# Revit family: Shower-Valve_Trim-KOHLER-K-26347T_1
name_source: partatom
category: Specialty Equipment
revit_build: Autodesk Revit 2017 (Build: 20160225_1515(x64)
units: mm (PartAtom-declared; Revit-internal decimal feet)

## family parameters
Cut with Voids When Loaded = No
Host = Face
OmniClass Number = 23.31.25.00
OmniClass Title = Toilet and Bath Specialties
Part Type = Normal
Room Calculation Point = No
Round Connector Dimension = Use Diameter
Shared = No

## types (6) — shared parameters
ADA Compliant = No
Assembly Code = C1030200
Date Modified = 02/12/2021
Default Elevation = 42"
Description = RECESSED THERMOSTATIC TRIM-3-OUTLET
Height = 4 1/16"
Length = 2 9/16"
Manufacturer = KOHLER Co.
Master Format 2014 = 10 28 00
Master Format 2014 Name = Toilet, Bath, and Laundry Accessories
Material = Premium Metal Construction
URL = http://www.kohler.com.cn
WaterSense Certified = No
Width = 13 5/16"

## per-type parameters (varying)
| type | Finish | Model | Type |
| CP- Polished Chrome | Kohler-Metal-CP-Polished_Chrome | K-26347T-9-CP | 1 |
| AF- Flange Gold | Kohler-Metal-AF-Flange_Gold | K-26347T-9-AF | 2 |
| BL-Primary Black | Kohler-Metal-BL-Matte_Black | K-26347T-9-BL | 3 |
| 2MB- Vibrant Brushed Moderne Brass | Kohler-Metal-2MB-Vibrant_Brushed_Moderne_Brass | K-26347T-9-2MB | 4 |
| RGD- Rose Gold | Kohler-Metal-RGD-Rose_Gold | K-26347T-9-RGD | 5 |
| BN- Roman Silver | Kohler-Metal-BN-Roman_Silver | K-26347T-9-BN | 6 |

## geometry (parser evidence)
native form markers: Sweep x6
no freeform markers — native parametric forms only
